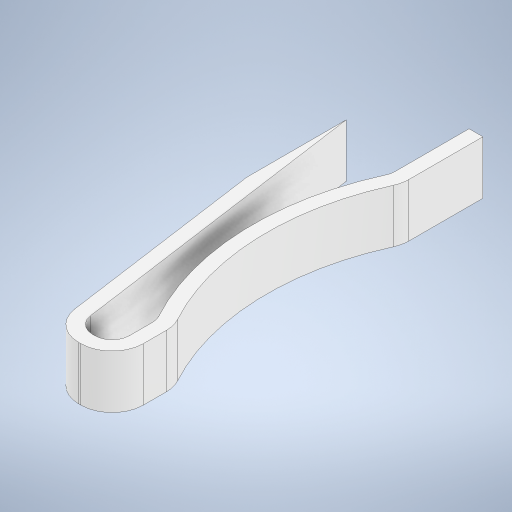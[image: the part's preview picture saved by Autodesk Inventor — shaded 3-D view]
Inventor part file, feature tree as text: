
AUTODESK INVENTOR PART (.ipt)
format: ipt  version: 2024 (Build 280153000, 153)  size: 550,400 bytes
history: native  units: in
note: dims shown in document units (in); Inventor stores cm internally (conversion verified against a paired STEP export)
features: extrude x4, sketch x2, other x1, plane x1, mirror x1, shell x1, projected_geometry x1, fillet x1
ambient origin geometry x8: Origin, YZ Plane, XZ Plane, XY Plane, X Axis, Y Axis, Z Axis, Center Point
bodies: Solid1 (feature_tree)
feature tree (12):
  other  "Plane1"
  sketch  "Sketch1"  dims[d10=0.0787in d11=0.0787in]
  extrude  "Extrusion1"  Depth=0.0787in
  extrude  "Extrusion2"  Depth=0.0787in
  plane  "Work Plane2"
  extrude  "Extrusion3"  TaperAngle=0.0deg  [1 undecoded]
  extrude  "Extrusion4"  TaperAngle=0.0deg  [1 undecoded]
  mirror  "Mirror1"
  shell  "Shell1"  Thickness=0.035in
  projected_geometry  "Projected Loop1"
  sketch  "Sketch2"  dims[d12=45.0deg d13=0.0414in d14=0.0in d15=0.0in d16=0.035in d17=0.0461in d18=0.0242in d19=0.0108in d20=0.035in d21=0.1969in d22=0.1969in d23=0.0134in d24=0.0423in d25=0.0in d26=0.0in d27=0.3937in d28=0.0in d29=0.0846in d30=0.0846in d31=0.3937in d32=0.0in d33=0.0394in d34=0.0394in d35=0.0in d36=0.0in d37=0.0787in]
  fillet  "Fillet1"  Radius=0.0461in
note: 2 required parameter values undecoded (feature->parameter linkage not recoverable at this tier; creation-order binding heuristic only, values carry confidence <= 0.55)
